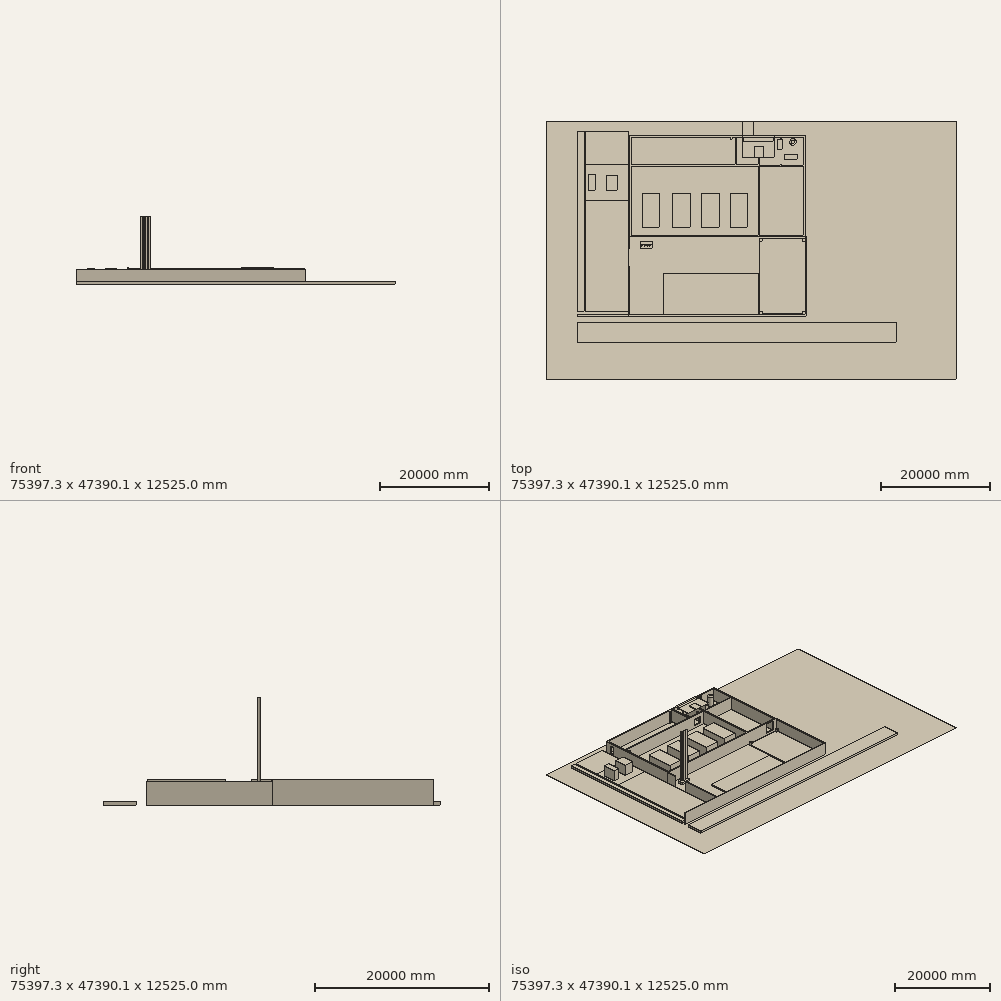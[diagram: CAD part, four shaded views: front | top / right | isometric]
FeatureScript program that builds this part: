
annotation { "Feature Type Name" : "Feature", "Feature Type Description" : "" }
export const myFeature = defineFeature(function(context is Context, id is Id, definition is map)
    precondition{}
    {
        {
            var Q0;
            Q0=qCreatedBy(makeId("Top.planeOp"),FACE);
            var sketch = newSketch(context, id + "F0", { "sketchPlane" : qUnion([Q0])});
            skLineSegment(sketch, "E0.bottom", {"start": v(0, 0) * mm, "end": v(75397.33, 0) * mm});
            skLineSegment(sketch, "E0.top", {"start": v(0, 47390.05) * mm, "end": v(75397.33, 47390.05) * mm});
            skLineSegment(sketch, "E0.left", {"start": v(0, 0) * mm, "end": v(0, 47390.05) * mm});
            skLineSegment(sketch, "E0.right", {"start": v(75397.33, 0) * mm, "end": v(75397.33, 47390.05) * mm});
            skSolve(sketch);
        }
        {
            var Q0;
            Q0 = qSketchRegion(id + "F0", true);
            var Q1;
            Q1=sQuery(id+"F0.wireOp",EDGE,"E0.top");
            var Q2;
            Q2=sQuery(id+"F0.wireOp",EDGE,"E0.left");
            var Q3;
            Q3=sQuery(id+"F0.wireOp",EDGE,"E0.bottom");
            var Q4;
            Q4=sQuery(id+"F0.wireOp",EDGE,"E0.right");
            extrude(context, id + "F1", {"entities" : qUnion([Q0]), "surfaceEntities" : qUnion([Q1, Q2, Q3, Q4]), "depth" : 25 * mm, "offsetDistance" : 25 * mm});
        }
        {
            var Q0;
            Q0=makeQuery(id+"F1.opExtrude","CAP_FACE",FACE,{"disambiguationData":[OSD([sQuery(id+"F0.wireOp",EDGE,"E0.bottom"),sQuery(id+"F0.wireOp",EDGE,"E0.top"),sQuery(id+"F0.wireOp",EDGE,"E0.left"),sQuery(id+"F0.wireOp",EDGE,"E0.right")])],"isStart":false});
            var sketch = newSketch(context, id + "F2", { "sketchPlane" : qUnion([Q0])});
            skLineSegment(sketch, "E1.top", {"start": v(15550.39, 26489.85) * mm, "end": v(38950.39, 26489.85) * mm});
            skLineSegment(sketch, "E1.left", {"start": v(15250.39, 44489.85) * mm, "end": v(15250.39, 39489.85) * mm});
            skLineSegment(sketch, "E1.right", {"start": v(47250.39, 44489.85) * mm, "end": v(47250.39, 26489.85) * mm});
            skLineSegment(sketch, "E2", {"start": v(39250.39, 26489.85) * mm, "end": v(39250.39, 44489.85) * mm});
            skLineSegment(sketch, "E3", {"start": v(15550.39, 39489.85) * mm, "end": v(38950.39, 39489.85) * mm});
            skLineSegment(sketch, "E4", {"start": v(5738.33, 45652.55) * mm, "end": v(5738.33, 12489.85) * mm});
            skLineSegment(sketch, "E5", {"start": v(6911.72, 12489.85) * mm, "end": v(5738.33, 12489.85) * mm});
            skLineSegment(sketch, "E6", {"start": v(5684.42, 10489.85) * mm, "end": v(64413.56, 10489.85) * mm});
            skLineSegment(sketch, "E7", {"start": v(5684.42, 6686.74) * mm, "end": v(64413.56, 6686.74) * mm});
            skLineSegment(sketch, "E8", {"start": v(5684.42, 10489.85) * mm, "end": v(5684.42, 6686.74) * mm});
            skLineSegment(sketch, "E9", {"start": v(64413.56, 10489.85) * mm, "end": v(64413.56, 6686.74) * mm});
            skLineSegment(sketch, "E10", {"start": v(39250.39, 44489.85) * mm, "end": v(47250.39, 44489.85) * mm});
            skLineSegment(sketch, "E11.trimOffspring", {"start": v(39250.39, 26489.85) * mm, "end": v(47250.39, 26489.85) * mm});
            skLineSegment(sketch, "E12", {"start": v(38950.39, 44489.85) * mm, "end": v(15550.39, 44489.85) * mm});
            skLineSegment(sketch, "E13", {"start": v(15550.39, 39189.85) * mm, "end": v(38950.39, 39189.85) * mm});
            skLineSegment(sketch, "E14.trimOffspring", {"start": v(38950.39, 39489.85) * mm, "end": v(38950.39, 44489.85) * mm});
            skLineSegment(sketch, "E15.trimOffspring", {"start": v(15250.39, 39189.85) * mm, "end": v(15250.39, 26489.85) * mm});
            skLineSegment(sketch, "E16.left", {"start": v(6911.72, 45652.55) * mm, "end": v(6911.72, 12489.85) * mm});
            skLineSegment(sketch, "E17.trimOffspring", {"start": v(5738.33, 45652.55) * mm, "end": v(6911.72, 45652.55) * mm});
            skLineSegment(sketch, "E18", {"start": v(15100.39, 12489.85) * mm, "end": v(15100.39, 45621.21) * mm});
            skLineSegment(sketch, "E19.right", {"start": v(8381.05, 13854.85) * mm, "end": v(8381.05, 13847.74) * mm});
            skLineSegment(sketch, "E20.top", {"start": v(15250.39, 44789.85) * mm, "end": v(47550.39, 44789.85) * mm});
            skLineSegment(sketch, "E21", {"start": v(15250.39, 26189.85) * mm, "end": v(15250.39, 44789.85) * mm});
            skLineSegment(sketch, "E22", {"start": v(7100.39, 45621.21) * mm, "end": v(15100.39, 45621.21) * mm});
            skLineSegment(sketch, "E23.trimOffspring", {"start": v(7100.39, 45621.21) * mm, "end": v(7100.39, 12489.85) * mm});
            skLineSegment(sketch, "E24", {"start": v(7100.39, 12489.85) * mm, "end": v(15100.39, 12489.85) * mm});
            skLineSegment(sketch, "E25", {"start": v(39250.39, 39189.85) * mm, "end": v(39250.39, 26489.85) * mm});
            skLineSegment(sketch, "E26", {"start": v(47550.39, 44789.85) * mm, "end": v(47550.39, 26189.85) * mm});
            skLineSegment(sketch, "E27", {"start": v(47550.39, 26189.85) * mm, "end": v(15250.39, 26189.85) * mm});
            skLineSegment(sketch, "E28", {"start": v(38950.39, 26489.85) * mm, "end": v(38950.39, 39189.85) * mm});
            skLineSegment(sketch, "E29", {"start": v(15550.39, 26489.85) * mm, "end": v(15550.39, 39189.85) * mm});
            skLineSegment(sketch, "E30", {"start": v(15550.39, 44489.85) * mm, "end": v(15550.39, 39489.85) * mm});
            skLineSegment(sketch, "E31.bottom", {"start": v(17308.66, 25290.44) * mm, "end": v(19540.62, 25290.44) * mm});
            skLineSegment(sketch, "E31.top", {"start": v(17308.66, 23988.97) * mm, "end": v(19540.62, 23988.97) * mm});
            skLineSegment(sketch, "E31.left", {"start": v(17308.66, 25290.44) * mm, "end": v(17308.66, 23988.97) * mm});
            skLineSegment(sketch, "E31.right", {"start": v(19540.62, 25290.44) * mm, "end": v(19540.62, 23988.97) * mm});
            skSolve(sketch);
        }
        {
            var Q0;
            Q0=makeQuery(id+"F2.imprint","IMPRINT",FACE,{"disambiguationData":[TD([[makeQuery(id+"F2.imprint","IMPRINT",EDGE,{"derivedFrom":sQuery(id+"F2.wireOp",EDGE,"E1.top")}),-1.0]])]});
            extrude(context, id + "F3", {"entities" : qUnion([Q0]), "operationType" : NewBodyOperationType.ADD, "depth" : 3000 * mm, "offsetDistance" : 25 * mm});
        }
        {
            var Q0;
            {var subQ0=sQuery(id+"F0.wireOp",EDGE,"E0.left");var subQ1=sQuery(id+"F0.wireOp",EDGE,"E0.top");var subQ2=sQuery(id+"F0.wireOp",EDGE,"E0.right");var subQ3=sQuery(id+"F0.wireOp",EDGE,"E0.bottom");Q0=makeQuery(id+"F3.boolean.opBoolean","SPLIT",FACE,{"disambiguationData":[TD([makeQuery(id+"F1.opExtrude","SWEPT_FACE",FACE,{"disambiguationData":[OSD([subQ3])]})])],"derivedFrom":makeQuery(id+"F1.opExtrude","CAP_FACE",FACE,{"disambiguationData":[OSD([subQ3,subQ1,subQ0,subQ2])],"isStart":false})});}
            var sketch = newSketch(context, id + "F4", { "sketchPlane" : qUnion([Q0])});
            skLineSegment(sketch, "E32.bottom", {"start": v(47550.39, 25889.85) * mm, "end": v(39250.39, 25889.85) * mm});
            skLineSegment(sketch, "E32.top", {"start": v(47550.39, 11889.85) * mm, "end": v(39250.39, 11889.85) * mm});
            skLineSegment(sketch, "E32.left", {"start": v(47550.39, 25889.85) * mm, "end": v(47550.39, 11889.85) * mm});
            skLineSegment(sketch, "E32.right", {"start": v(39250.39, 25889.85) * mm, "end": v(39250.39, 11889.85) * mm});
            skSolve(sketch);
        }
        {
            var Q0;
            Q0=makeQuery(id+"F4.imprint","IMPRINT",FACE,{"disambiguationData":[TD([[makeQuery(id+"F4.imprint","IMPRINT",EDGE,{"derivedFrom":sQuery(id+"F4.wireOp",EDGE,"E32.bottom")}),1.0]])]});
            var Q1;
            Q1=sQuery(id+"F4.wireOp",EDGE,"E32.right");
            var Q2;
            Q2=sQuery(id+"F4.wireOp",EDGE,"E32.top");
            var Q3;
            Q3=sQuery(id+"F4.wireOp",EDGE,"E32.left");
            var Q4;
            Q4=sQuery(id+"F4.wireOp",EDGE,"E32.bottom");
            extrude(context, id + "F5", {"entities" : qUnion([Q0]), "surfaceEntities" : qUnion([Q1, Q2, Q3, Q4]), "depth" : 200 * mm, "offsetDistance" : 25 * mm});
        }
        {
            var Q0;
            Q0 = qSketchRegion(id + "F2", true);
            var Q1;
            {var subQ0=sQuery(id+"F0.wireOp",EDGE,"E0.left");var subQ1=sQuery(id+"F0.wireOp",EDGE,"E0.top");var subQ2=sQuery(id+"F0.wireOp",EDGE,"E0.right");var subQ3=sQuery(id+"F0.wireOp",EDGE,"E0.bottom");Q1=makeQuery(id+"F3.boolean.opBoolean","SPLIT",FACE,{"disambiguationData":[TD([makeQuery(id+"F1.opExtrude","SWEPT_FACE",FACE,{"disambiguationData":[OSD([subQ3])]})])],"derivedFrom":makeQuery(id+"F1.opExtrude","CAP_FACE",FACE,{"disambiguationData":[OSD([subQ3,subQ1,subQ0,subQ2])],"isStart":false})});}
            extrude(context, id + "F6", {"entities" : qUnion([Q0, Q1]), "operationType" : NewBodyOperationType.ADD, "depth" : 25 * mm, "offsetDistance" : 25 * mm});
        }
        {
            var Q0;
            Q0 = qSketchRegion(id + "F2", true);
            extrude(context, id + "F7", {"entities" : qUnion([Q0]), "operationType" : NewBodyOperationType.ADD, "depth" : 200 * mm, "offsetDistance" : 25 * mm});
        }
        {
            var Q0;
            {var subQ0=sQuery(id+"F2.wireOp",EDGE,"d6d11424-035c-424b-929e-fb8eabbb2fd0.right");var subQ1=sQuery(id+"F2.wireOp",EDGE,"d6d11424-035c-424b-929e-fb8eabbb2fd0.bottom");var subQ2=sQuery(id+"F2.wireOp",EDGE,"E9");var subQ3=sQuery(id+"F2.wireOp",EDGE,"E8");var subQ4=sQuery(id+"F2.wireOp",EDGE,"E7");var subQ5=sQuery(id+"F2.wireOp",EDGE,"E6");var subQ6=sQuery(id+"F2.wireOp",EDGE,"E5");var subQ7=sQuery(id+"F0.wireOp",EDGE,"E0.right");var subQ8=sQuery(id+"F2.wireOp",EDGE,"d6d11424-035c-424b-929e-fb8eabbb2fd0.left");var subQ9=sQuery(id+"F2.wireOp",EDGE,"E27");var subQ10=sQuery(id+"F2.wireOp",EDGE,"E16.left");var subQ11=sQuery(id+"F2.wireOp",EDGE,"d6d11424-035c-424b-929e-fb8eabbb2fd0.top");var subQ12=sQuery(id+"F2.wireOp",EDGE,"E26");var subQ13=sQuery(id+"F0.wireOp",EDGE,"E0.left");var subQ14=sQuery(id+"F0.wireOp",EDGE,"E0.bottom");var subQ15=sQuery(id+"F2.wireOp",EDGE,"E4");var subQ16=sQuery(id+"F2.wireOp",EDGE,"E24");var subQ17=sQuery(id+"F0.wireOp",EDGE,"E0.top");var subQ18=sQuery(id+"F2.wireOp",EDGE,"E20.top");var subQ19=sQuery(id+"F2.wireOp",EDGE,"E21");var subQ20=sQuery(id+"F2.wireOp",EDGE,"E23.trimOffspring");var subQ21=sQuery(id+"F2.wireOp",EDGE,"E17.trimOffspring");var subQ22=sQuery(id+"F2.wireOp",EDGE,"E18");var subQ23=sQuery(id+"F2.wireOp",EDGE,"E22");Q0=makeQuery(id+"F7.boolean.opBoolean","SPLIT",FACE,{"disambiguationData":[TD([makeQuery(id+"F1.opExtrude","SWEPT_FACE",FACE,{"disambiguationData":[OSD([subQ14])]})])],"derivedFrom":makeQuery(id+"F6.boolean.opBoolean","MERGE",FACE,{"derivedFrom":[makeQuery(id+"F6.opExtrude","CAP_FACE",FACE,{"disambiguationData":[OSD([sQuery(id+"F2.wireOp",EDGE,"E1.top"),sQuery(id+"F2.wireOp",EDGE,"E1.right"),sQuery(id+"F2.wireOp",EDGE,"E2"),sQuery(id+"F2.wireOp",EDGE,"E3"),sQuery(id+"F2.wireOp",EDGE,"E10"),sQuery(id+"F2.wireOp",EDGE,"E11.trimOffspring"),sQuery(id+"F2.wireOp",EDGE,"E12"),sQuery(id+"F2.wireOp",EDGE,"E13"),sQuery(id+"F2.wireOp",EDGE,"E14.trimOffspring"),subQ18,subQ19,sQuery(id+"F2.wireOp",EDGE,"E25"),subQ12,subQ9,sQuery(id+"F2.wireOp",EDGE,"E28"),sQuery(id+"F2.wireOp",EDGE,"E29"),sQuery(id+"F2.wireOp",EDGE,"E30")])],"isStart":false}),makeQuery(id+"F6.opExtrude","CAP_FACE",FACE,{"disambiguationData":[OSD([subQ15,subQ6,subQ10,subQ21])],"isStart":false}),makeQuery(id+"F6.opExtrude","CAP_FACE",FACE,{"disambiguationData":[OSD([subQ5,subQ4,subQ3,subQ2])],"isStart":false}),makeQuery(id+"F6.opExtrude","CAP_FACE",FACE,{"disambiguationData":[OSD([subQ1,subQ11,subQ8,subQ0,sQuery(id+"F2.wireOp",EDGE,"95qXsgm3-6lwU-iEXp-UI7w-R3bsq3icprrx.bottom"),sQuery(id+"F2.wireOp",EDGE,"95qXsgm3-6lwU-iEXp-UI7w-R3bsq3icprrx.top"),sQuery(id+"F2.wireOp",EDGE,"95qXsgm3-6lwU-iEXp-UI7w-R3bsq3icprrx.left"),sQuery(id+"F2.wireOp",EDGE,"95qXsgm3-6lwU-iEXp-UI7w-R3bsq3icprrx.right")])],"isStart":false}),makeQuery(id+"F6.opExtrude","CAP_FACE",FACE,{"disambiguationData":[OSD([subQ22,subQ23,subQ20,subQ16])],"isStart":false}),makeQuery(id+"F6.opExtrude","CAP_FACE",FACE,{"disambiguationData":[OSD([subQ14,subQ17,subQ13,subQ7])],"isStart":false})]})});}
            var sketch = newSketch(context, id + "F8", { "sketchPlane" : qUnion([Q0])});
            skLineSegment(sketch, "E33.bottom", {"start": v(38899.38, 19555.93) * mm, "end": v(21486.93, 19555.93) * mm});
            skLineSegment(sketch, "E33.top", {"start": v(38899.38, 11971.84) * mm, "end": v(21486.93, 11971.84) * mm});
            skLineSegment(sketch, "E33.left", {"start": v(38899.38, 19555.93) * mm, "end": v(38899.38, 11971.84) * mm});
            skLineSegment(sketch, "E33.right", {"start": v(21486.93, 19555.93) * mm, "end": v(21486.93, 11971.84) * mm});
            skSolve(sketch);
        }
        {
            var Q0;
            Q0 = qSketchRegion(id + "F8", true);
            extrude(context, id + "F9", {"entities" : qUnion([Q0]), "operationType" : NewBodyOperationType.ADD, "depth" : 200 * mm, "offsetDistance" : 25 * mm});
        }
        {
            var Q0;
            Q0=makeQuery(id+"F3.opExtrude","SWEPT_FACE",FACE,{"disambiguationData":[OSD([sQuery(id+"F2.wireOp",EDGE,"E27")])]});
            var sketch = newSketch(context, id + "F10", { "sketchPlane" : qUnion([Q0])});
            skLineSegment(sketch, "E34.bottom", {"start": v(44814.1, 2729.8) * mm, "end": v(46814.1, 2729.8) * mm});
            skLineSegment(sketch, "E34.top", {"start": v(44814.1, 229.8) * mm, "end": v(46814.1, 229.8) * mm});
            skLineSegment(sketch, "E34.left", {"start": v(44814.1, 2729.8) * mm, "end": v(44814.1, 229.8) * mm});
            skLineSegment(sketch, "E34.right", {"start": v(46814.1, 2729.8) * mm, "end": v(46814.1, 229.8) * mm});
            skSolve(sketch);
        }
        {
            var Q0;
            Q0=makeQuery(id+"F10.imprint","IMPRINT",FACE,{"disambiguationData":[TD([[makeQuery(id+"F10.imprint","IMPRINT",EDGE,{"derivedFrom":sQuery(id+"F10.wireOp",EDGE,"E34.bottom")}),-1.0]])]});
            extrude(context, id + "F11", {"entities" : qUnion([Q0]), "operationType" : NewBodyOperationType.REMOVE, "oppositeDirection" : true, "depth" : 400 * mm, "offsetDistance" : 25 * mm});
        }
        {
            var Q0;
            Q0=makeQuery(id+"F3.opExtrude","SWEPT_FACE",FACE,{"disambiguationData":[OSD([sQuery(id+"F2.wireOp",EDGE,"E2"),sQuery(id+"F2.wireOp",EDGE,"E25")])]});
            var sketch = newSketch(context, id + "F12", { "sketchPlane" : qUnion([Q0])});
            skLineSegment(sketch, "E35.bottom", {"start": v(40270.04, 2225) * mm, "end": v(41470.04, 2225) * mm});
            skLineSegment(sketch, "E35.top", {"start": v(40270.04, 25) * mm, "end": v(41470.04, 25) * mm});
            skLineSegment(sketch, "E35.left", {"start": v(40270.04, 2225) * mm, "end": v(40270.04, 25) * mm});
            skLineSegment(sketch, "E35.right", {"start": v(41470.04, 2225) * mm, "end": v(41470.04, 25) * mm});
            skSolve(sketch);
        }
        {
            var Q0;
            Q0 = qSketchRegion(id + "F12", true);
            extrude(context, id + "F13", {"entities" : qUnion([Q0]), "operationType" : NewBodyOperationType.REMOVE, "oppositeDirection" : true, "depth" : 310 * mm, "offsetDistance" : 25 * mm});
        }
        {
            var Q0;
            Q0=makeQuery(id+"F3.opExtrude","SWEPT_FACE",FACE,{"disambiguationData":[OSD([sQuery(id+"F2.wireOp",EDGE,"E21")])]});
            var sketch = newSketch(context, id + "F14", { "sketchPlane" : qUnion([Q0])});
            skLineSegment(sketch, "E36.bottom", {"start": v(-43520.03, 2405.42) * mm, "end": v(-42542.72, 2405.42) * mm});
            skLineSegment(sketch, "E36.top", {"start": v(-43520.03, 220.95) * mm, "end": v(-42542.72, 220.95) * mm});
            skLineSegment(sketch, "E36.left", {"start": v(-43520.03, 2405.42) * mm, "end": v(-43520.03, 220.95) * mm});
            skLineSegment(sketch, "E36.right", {"start": v(-42542.72, 2405.42) * mm, "end": v(-42542.72, 220.95) * mm});
            skSolve(sketch);
        }
        {
            var Q0;
            Q0 = qSketchRegion(id + "F14", true);
            extrude(context, id + "F15", {"entities" : qUnion([Q0]), "operationType" : NewBodyOperationType.REMOVE, "oppositeDirection" : true, "depth" : 305 * mm, "offsetDistance" : 25 * mm});
        }
        {
            var Q0;
            Q0=makeQuery(id+"F5.opExtrude","CAP_FACE",FACE,{"disambiguationData":[OSD([sQuery(id+"F4.wireOp",EDGE,"E32.bottom"),sQuery(id+"F4.wireOp",EDGE,"E32.top"),sQuery(id+"F4.wireOp",EDGE,"E32.left"),sQuery(id+"F4.wireOp",EDGE,"E32.right")])],"isStart":false});
            var sketch = newSketch(context, id + "F16", { "sketchPlane" : qUnion([Q0])});
            skLineSegment(sketch, "E37.bottom", {"start": v(47550.39, 11889.85) * mm, "end": v(47050.39, 11889.85) * mm});
            skLineSegment(sketch, "E37.top", {"start": v(47550.39, 12389.85) * mm, "end": v(47050.39, 12389.85) * mm});
            skLineSegment(sketch, "E37.left", {"start": v(47550.39, 11889.85) * mm, "end": v(47550.39, 12389.85) * mm});
            skLineSegment(sketch, "E37.right", {"start": v(47050.39, 11889.85) * mm, "end": v(47050.39, 12389.85) * mm});
            skLineSegment(sketch, "E38.bottom", {"start": v(39250.39, 11889.85) * mm, "end": v(39705.44, 11889.85) * mm});
            skLineSegment(sketch, "E38.top", {"start": v(39250.39, 12389.85) * mm, "end": v(39705.44, 12389.85) * mm});
            skLineSegment(sketch, "E38.left", {"start": v(39250.39, 11889.85) * mm, "end": v(39250.39, 12389.85) * mm});
            skLineSegment(sketch, "E38.right", {"start": v(39705.44, 11889.85) * mm, "end": v(39705.44, 12389.85) * mm});
            skLineSegment(sketch, "E39.bottom", {"start": v(39250.39, 25889.85) * mm, "end": v(39750.39, 25889.85) * mm});
            skLineSegment(sketch, "E39.top", {"start": v(39250.39, 25389.85) * mm, "end": v(39750.39, 25389.85) * mm});
            skLineSegment(sketch, "E39.left", {"start": v(39250.39, 25889.85) * mm, "end": v(39250.39, 25389.85) * mm});
            skLineSegment(sketch, "E39.right", {"start": v(39750.39, 25889.85) * mm, "end": v(39750.39, 25389.85) * mm});
            skLineSegment(sketch, "E40.bottom", {"start": v(47550.39, 25889.85) * mm, "end": v(47050.39, 25889.85) * mm});
            skLineSegment(sketch, "E40.top", {"start": v(47550.39, 25389.85) * mm, "end": v(47050.39, 25389.85) * mm});
            skLineSegment(sketch, "E40.left", {"start": v(47550.39, 25889.85) * mm, "end": v(47550.39, 25389.85) * mm});
            skLineSegment(sketch, "E40.right", {"start": v(47050.39, 25889.85) * mm, "end": v(47050.39, 25389.85) * mm});
            skSolve(sketch);
        }
        {
            var Q0;
            Q0 = qSketchRegion(id + "F16", true);
            extrude(context, id + "F17", {"entities" : qUnion([Q0]), "operationType" : NewBodyOperationType.ADD, "depth" : 600 * mm, "offsetDistance" : 25 * mm});
        }
        {
            var Q0;
            Q0=makeQuery(id+"F3.opExtrude","SWEPT_FACE",FACE,{"disambiguationData":[OSD([sQuery(id+"F2.wireOp",EDGE,"E13")])]});
            var sketch = newSketch(context, id + "F18", { "sketchPlane" : qUnion([Q0])});
            skLineSegment(sketch, "E41.bottom", {"start": v(15908.28, 25) * mm, "end": v(16820.83, 25) * mm});
            skLineSegment(sketch, "E41.top", {"start": v(15908.28, 2525) * mm, "end": v(16820.83, 2525) * mm});
            skLineSegment(sketch, "E41.left", {"start": v(15908.28, 25) * mm, "end": v(15908.28, 2525) * mm});
            skLineSegment(sketch, "E41.right", {"start": v(16820.83, 25) * mm, "end": v(16820.83, 2525) * mm});
            skSolve(sketch);
        }
        {
            var Q0;
            Q0 = qSketchRegion(id + "F18", true);
            extrude(context, id + "F19", {"entities" : qUnion([Q0]), "operationType" : NewBodyOperationType.REMOVE, "oppositeDirection" : true, "depth" : 310 * mm, "offsetDistance" : 25 * mm});
        }
        {
            var Q0;
            {var subQ0=makeQuery(id+"F1.opExtrude","CAP_FACE",FACE,{"disambiguationData":[OSD([sQuery(id+"F0.wireOp",EDGE,"E0.bottom"),sQuery(id+"F0.wireOp",EDGE,"E0.top"),sQuery(id+"F0.wireOp",EDGE,"E0.left"),sQuery(id+"F0.wireOp",EDGE,"E0.right")])],"isStart":false});Q0=makeQuery(id+"F19.boolean.opBoolean","MERGE",FACE,{"derivedFrom":[makeQuery(id+"F3.boolean.opBoolean","SPLIT",FACE,{"disambiguationData":[TD([makeQuery(id+"F3.opExtrude","SWEPT_FACE",FACE,{"disambiguationData":[OSD([sQuery(id+"F2.wireOp",EDGE,"E1.top")])]})])],"derivedFrom":subQ0}),makeQuery(id+"F13.boolean.opBoolean","MERGE",FACE,{"derivedFrom":[makeQuery(id+"F3.boolean.opBoolean","SPLIT",FACE,{"disambiguationData":[TD([makeQuery(id+"F3.opExtrude","SWEPT_FACE",FACE,{"disambiguationData":[OSD([sQuery(id+"F2.wireOp",EDGE,"E1.right")])]})])],"derivedFrom":subQ0}),makeQuery(id+"F3.boolean.opBoolean","SPLIT",FACE,{"disambiguationData":[TD([makeQuery(id+"F3.opExtrude","SWEPT_FACE",FACE,{"disambiguationData":[OSD([sQuery(id+"F2.wireOp",EDGE,"E3")])]})])],"derivedFrom":subQ0}),makeQuery(id+"F13.opExtrude","SWEPT_FACE",FACE,{"disambiguationData":[OSD([sQuery(id+"F12.wireOp",EDGE,"E35.top")])]})]}),makeQuery(id+"F19.opExtrude","SWEPT_FACE",FACE,{"disambiguationData":[OSD([sQuery(id+"F18.wireOp",EDGE,"E41.bottom")])]})]});}
            var sketch = newSketch(context, id + "F20", { "sketchPlane" : qUnion([Q0])});
            skLineSegment(sketch, "E42.bottom", {"start": v(43250.39, 44489.85) * mm, "end": v(42950.39, 44489.85) * mm});
            skLineSegment(sketch, "E42.top", {"start": v(43250.39, 44189.85) * mm, "end": v(42950.39, 44189.85) * mm});
            skLineSegment(sketch, "E42.left", {"start": v(43250.39, 44489.85) * mm, "end": v(43250.39, 44189.85) * mm});
            skLineSegment(sketch, "E42.right", {"start": v(42950.39, 44489.85) * mm, "end": v(42950.39, 44189.85) * mm});
            skLineSegment(sketch, "E43.bottom", {"start": v(43250.39, 39511.55) * mm, "end": v(42950.39, 39511.55) * mm});
            skLineSegment(sketch, "E43.top", {"start": v(43250.39, 39211.55) * mm, "end": v(42950.39, 39211.55) * mm});
            skLineSegment(sketch, "E43.left", {"start": v(43250.39, 39511.55) * mm, "end": v(43250.39, 39211.55) * mm});
            skLineSegment(sketch, "E43.right", {"start": v(42950.39, 39511.55) * mm, "end": v(42950.39, 39211.55) * mm});
            skLineSegment(sketch, "E44.bottom", {"start": v(33845.83, 39511.55) * mm, "end": v(34145.83, 39511.55) * mm});
            skLineSegment(sketch, "E44.top", {"start": v(33845.83, 39211.55) * mm, "end": v(34145.83, 39211.55) * mm});
            skLineSegment(sketch, "E44.left", {"start": v(33845.83, 39511.55) * mm, "end": v(33845.83, 39211.55) * mm});
            skLineSegment(sketch, "E44.right", {"start": v(34145.83, 39511.55) * mm, "end": v(34145.83, 39211.55) * mm});
            skLineSegment(sketch, "E45.bottom", {"start": v(33845.83, 44489.85) * mm, "end": v(34145.83, 44489.85) * mm});
            skLineSegment(sketch, "E45.top", {"start": v(33845.83, 44189.85) * mm, "end": v(34145.83, 44189.85) * mm});
            skLineSegment(sketch, "E45.left", {"start": v(33845.83, 44489.85) * mm, "end": v(33845.83, 44189.85) * mm});
            skLineSegment(sketch, "E45.right", {"start": v(34145.83, 44489.85) * mm, "end": v(34145.83, 44189.85) * mm});
            skSolve(sketch);
        }
        {
            var Q0;
            Q0=makeQuery(id+"F20.imprint","IMPRINT",FACE,{"disambiguationData":[TD([[makeQuery(id+"F20.imprint","IMPRINT",EDGE,{"derivedFrom":sQuery(id+"F20.wireOp",EDGE,"E42.bottom")}),-1.0]])]});
            var Q1;
            Q1=makeQuery(id+"F20.imprint","IMPRINT",FACE,{"disambiguationData":[TD([[makeQuery(id+"F20.imprint","IMPRINT",EDGE,{"derivedFrom":sQuery(id+"F20.wireOp",EDGE,"E43.bottom")}),1.0]])]});
            var Q2;
            {var subQ0=sQuery(id+"F20.wireOp",EDGE,"E44.bottom");Q2=makeQuery(id+"F20.imprint","IMPRINT",FACE,{"disambiguationData":[TD([[makeQuery(id+"F20.imprint","IMPRINT",EDGE,{"derivedFrom":subQ0}),-1.0]])]});}
            var Q3;
            Q3=makeQuery(id+"F20.imprint","IMPRINT",FACE,{"disambiguationData":[TD([[makeQuery(id+"F20.imprint","IMPRINT",EDGE,{"derivedFrom":sQuery(id+"F20.wireOp",EDGE,"E45.bottom")}),1.0]])]});
            extrude(context, id + "F21", {"entities" : qUnion([Q0, Q1, Q2, Q3]), "operationType" : NewBodyOperationType.ADD, "depth" : 3000 * mm, "offsetDistance" : 25 * mm});
        }
        {
            var Q0;
            Q0=makeQuery(id+"F3.opExtrude","SWEPT_FACE",FACE,{"disambiguationData":[OSD([sQuery(id+"F2.wireOp",EDGE,"E13")])]});
            var sketch = newSketch(context, id + "F22", { "sketchPlane" : qUnion([Q0])});
            skLineSegment(sketch, "E46.bottom", {"start": v(35990.2, 2225) * mm, "end": v(37990.2, 2225) * mm});
            skLineSegment(sketch, "E46.top", {"start": v(35990.2, 25) * mm, "end": v(37990.2, 25) * mm});
            skLineSegment(sketch, "E46.left", {"start": v(35990.2, 2225) * mm, "end": v(35990.2, 25) * mm});
            skLineSegment(sketch, "E46.right", {"start": v(37990.2, 2225) * mm, "end": v(37990.2, 25) * mm});
            skSolve(sketch);
        }
        {
            var Q0;
            Q0 = qSketchRegion(id + "F22", true);
            extrude(context, id + "F23", {"entities" : qUnion([Q0]), "operationType" : NewBodyOperationType.REMOVE, "endBound" : BoundingType.THROUGH_ALL, "oppositeDirection" : true, "depth" : 25 * mm, "offsetDistance" : 25 * mm});
        }
        {
            var Q0;
            Q0=makeQuery(id+"F5.opExtrude","CAP_FACE",FACE,{"disambiguationData":[OSD([sQuery(id+"F4.wireOp",EDGE,"E32.bottom"),sQuery(id+"F4.wireOp",EDGE,"E32.top"),sQuery(id+"F4.wireOp",EDGE,"E32.left"),sQuery(id+"F4.wireOp",EDGE,"E32.right")])],"isStart":false});
            var sketch = newSketch(context, id + "F24", { "sketchPlane" : qUnion([Q0])});
            skLineSegment(sketch, "E47.bottom", {"start": v(39705.44, 12139.85) * mm, "end": v(47050.39, 12139.85) * mm});
            skLineSegment(sketch, "E47.top", {"start": v(39705.44, 12139.85) * mm, "end": v(47050.39, 12139.85) * mm});
            skLineSegment(sketch, "E47.left", {"start": v(39705.44, 12139.85) * mm, "end": v(39705.44, 12139.85) * mm});
            skLineSegment(sketch, "E47.right", {"start": v(47050.39, 12139.85) * mm, "end": v(47050.39, 12139.85) * mm});
            skLineSegment(sketch, "E48.bottom", {"start": v(47050.39, 11889.85) * mm, "end": v(39705.44, 11889.85) * mm});
            skLineSegment(sketch, "E48.top", {"start": v(47050.39, 12139.85) * mm, "end": v(39705.44, 12139.85) * mm});
            skLineSegment(sketch, "E48.left", {"start": v(47050.39, 11889.85) * mm, "end": v(47050.39, 12139.85) * mm});
            skLineSegment(sketch, "E48.right", {"start": v(39705.44, 11889.85) * mm, "end": v(39705.44, 12139.85) * mm});
            skSolve(sketch);
        }
        {
            var Q0;
            Q0 = qSketchRegion(id + "F24", true);
            var Q1;
            Q1=makeQuery(id+"F24.imprint","IMPRINT",FACE,{"disambiguationData":[TD([[makeQuery(id+"F24.imprint","IMPRINT",EDGE,{"derivedFrom":sQuery(id+"F24.wireOp",EDGE,"E48.bottom")}),-1.0]])]});
            extrude(context, id + "F25", {"entities" : qUnion([Q0, Q1]), "operationType" : NewBodyOperationType.ADD, "depth" : 1000 * mm, "offsetDistance" : 25 * mm});
        }
        {
            var Q0;
            {var subQ0=sQuery(id+"F2.wireOp",EDGE,"d6d11424-035c-424b-929e-fb8eabbb2fd0.right");var subQ1=sQuery(id+"F2.wireOp",EDGE,"d6d11424-035c-424b-929e-fb8eabbb2fd0.bottom");var subQ2=sQuery(id+"F2.wireOp",EDGE,"E9");var subQ3=sQuery(id+"F2.wireOp",EDGE,"E8");var subQ4=sQuery(id+"F2.wireOp",EDGE,"E7");var subQ5=sQuery(id+"F2.wireOp",EDGE,"E6");var subQ6=sQuery(id+"F2.wireOp",EDGE,"E5");var subQ7=sQuery(id+"F0.wireOp",EDGE,"E0.right");var subQ8=sQuery(id+"F2.wireOp",EDGE,"d6d11424-035c-424b-929e-fb8eabbb2fd0.left");var subQ9=sQuery(id+"F2.wireOp",EDGE,"E27");var subQ10=sQuery(id+"F2.wireOp",EDGE,"E16.left");var subQ11=sQuery(id+"F2.wireOp",EDGE,"d6d11424-035c-424b-929e-fb8eabbb2fd0.top");var subQ12=sQuery(id+"F2.wireOp",EDGE,"E26");var subQ13=sQuery(id+"F0.wireOp",EDGE,"E0.left");var subQ14=sQuery(id+"F0.wireOp",EDGE,"E0.bottom");var subQ15=sQuery(id+"F2.wireOp",EDGE,"E4");var subQ16=sQuery(id+"F2.wireOp",EDGE,"E24");var subQ17=sQuery(id+"F0.wireOp",EDGE,"E0.top");var subQ18=sQuery(id+"F2.wireOp",EDGE,"E20.top");var subQ19=sQuery(id+"F2.wireOp",EDGE,"E21");var subQ20=sQuery(id+"F2.wireOp",EDGE,"E23.trimOffspring");var subQ21=sQuery(id+"F2.wireOp",EDGE,"E17.trimOffspring");var subQ22=sQuery(id+"F2.wireOp",EDGE,"E18");var subQ23=sQuery(id+"F2.wireOp",EDGE,"E22");Q0=makeQuery(id+"F7.boolean.opBoolean","SPLIT",FACE,{"disambiguationData":[TD([makeQuery(id+"F1.opExtrude","SWEPT_FACE",FACE,{"disambiguationData":[OSD([subQ14])]})])],"derivedFrom":makeQuery(id+"F6.boolean.opBoolean","MERGE",FACE,{"derivedFrom":[makeQuery(id+"F6.opExtrude","CAP_FACE",FACE,{"disambiguationData":[OSD([sQuery(id+"F2.wireOp",EDGE,"E1.top"),sQuery(id+"F2.wireOp",EDGE,"E1.right"),sQuery(id+"F2.wireOp",EDGE,"E2"),sQuery(id+"F2.wireOp",EDGE,"E3"),sQuery(id+"F2.wireOp",EDGE,"E10"),sQuery(id+"F2.wireOp",EDGE,"E11.trimOffspring"),sQuery(id+"F2.wireOp",EDGE,"E12"),sQuery(id+"F2.wireOp",EDGE,"E13"),sQuery(id+"F2.wireOp",EDGE,"E14.trimOffspring"),subQ18,subQ19,sQuery(id+"F2.wireOp",EDGE,"E25"),subQ12,subQ9,sQuery(id+"F2.wireOp",EDGE,"E28"),sQuery(id+"F2.wireOp",EDGE,"E29"),sQuery(id+"F2.wireOp",EDGE,"E30")])],"isStart":false}),makeQuery(id+"F6.opExtrude","CAP_FACE",FACE,{"disambiguationData":[OSD([subQ15,subQ6,subQ10,subQ21])],"isStart":false}),makeQuery(id+"F6.opExtrude","CAP_FACE",FACE,{"disambiguationData":[OSD([subQ5,subQ4,subQ3,subQ2])],"isStart":false}),makeQuery(id+"F6.opExtrude","CAP_FACE",FACE,{"disambiguationData":[OSD([subQ1,subQ11,subQ8,subQ0,sQuery(id+"F2.wireOp",EDGE,"95qXsgm3-6lwU-iEXp-UI7w-R3bsq3icprrx.bottom"),sQuery(id+"F2.wireOp",EDGE,"95qXsgm3-6lwU-iEXp-UI7w-R3bsq3icprrx.top"),sQuery(id+"F2.wireOp",EDGE,"95qXsgm3-6lwU-iEXp-UI7w-R3bsq3icprrx.left"),sQuery(id+"F2.wireOp",EDGE,"95qXsgm3-6lwU-iEXp-UI7w-R3bsq3icprrx.right")])],"isStart":false}),makeQuery(id+"F6.opExtrude","CAP_FACE",FACE,{"disambiguationData":[OSD([subQ22,subQ23,subQ20,subQ16])],"isStart":false}),makeQuery(id+"F6.opExtrude","CAP_FACE",FACE,{"disambiguationData":[OSD([subQ14,subQ17,subQ13,subQ7])],"isStart":false})]})});}
            var sketch = newSketch(context, id + "F26", { "sketchPlane" : qUnion([Q0])});
            skLineSegment(sketch, "E49.bottom", {"start": v(47800.39, 11638.85) * mm, "end": v(5738.33, 11638.85) * mm});
            skLineSegment(sketch, "E49.top", {"start": v(47550.39, 11888.85) * mm, "end": v(5738.33, 11888.85) * mm});
            skLineSegment(sketch, "E49.left", {"start": v(47800.39, 11638.85) * mm, "end": v(47800.39, 11888.85) * mm});
            skLineSegment(sketch, "E49.right", {"start": v(5738.33, 11638.85) * mm, "end": v(5738.33, 11888.85) * mm});
            skLineSegment(sketch, "E50.bottom", {"start": v(47800.39, 11638.85) * mm, "end": v(47550.39, 11638.85) * mm});
            skLineSegment(sketch, "E50.top", {"start": v(47800.39, 26189.85) * mm, "end": v(47550.39, 26189.85) * mm});
            skLineSegment(sketch, "E50.left", {"start": v(47800.39, 11638.85) * mm, "end": v(47800.39, 26189.85) * mm});
            skLineSegment(sketch, "E50.right", {"start": v(47550.39, 11888.85) * mm, "end": v(47550.39, 26189.85) * mm});
            skSolve(sketch);
        }
        {
            var Q0;
            {var subQ0=sQuery(id+"F2.wireOp",EDGE,"d6d11424-035c-424b-929e-fb8eabbb2fd0.right");var subQ1=sQuery(id+"F2.wireOp",EDGE,"d6d11424-035c-424b-929e-fb8eabbb2fd0.bottom");var subQ2=sQuery(id+"F2.wireOp",EDGE,"E9");var subQ3=sQuery(id+"F2.wireOp",EDGE,"E8");var subQ4=sQuery(id+"F2.wireOp",EDGE,"E7");var subQ5=sQuery(id+"F2.wireOp",EDGE,"E6");var subQ6=sQuery(id+"F2.wireOp",EDGE,"E5");var subQ7=sQuery(id+"F0.wireOp",EDGE,"E0.right");var subQ8=sQuery(id+"F2.wireOp",EDGE,"d6d11424-035c-424b-929e-fb8eabbb2fd0.left");var subQ9=sQuery(id+"F2.wireOp",EDGE,"E27");var subQ10=sQuery(id+"F2.wireOp",EDGE,"E16.left");var subQ11=sQuery(id+"F2.wireOp",EDGE,"d6d11424-035c-424b-929e-fb8eabbb2fd0.top");var subQ12=sQuery(id+"F2.wireOp",EDGE,"E26");var subQ13=sQuery(id+"F0.wireOp",EDGE,"E0.left");var subQ14=sQuery(id+"F0.wireOp",EDGE,"E0.bottom");var subQ15=sQuery(id+"F2.wireOp",EDGE,"E4");var subQ16=sQuery(id+"F2.wireOp",EDGE,"E24");var subQ17=sQuery(id+"F0.wireOp",EDGE,"E0.top");var subQ18=sQuery(id+"F2.wireOp",EDGE,"E20.top");var subQ19=sQuery(id+"F2.wireOp",EDGE,"E21");var subQ20=sQuery(id+"F2.wireOp",EDGE,"E23.trimOffspring");var subQ21=sQuery(id+"F2.wireOp",EDGE,"E17.trimOffspring");var subQ22=sQuery(id+"F2.wireOp",EDGE,"E18");var subQ23=sQuery(id+"F2.wireOp",EDGE,"E22");Q0=makeQuery(id+"F7.boolean.opBoolean","SPLIT",FACE,{"disambiguationData":[TD([makeQuery(id+"F1.opExtrude","SWEPT_FACE",FACE,{"disambiguationData":[OSD([subQ14])]})])],"derivedFrom":makeQuery(id+"F6.boolean.opBoolean","MERGE",FACE,{"derivedFrom":[makeQuery(id+"F6.opExtrude","CAP_FACE",FACE,{"disambiguationData":[OSD([sQuery(id+"F2.wireOp",EDGE,"E1.top"),sQuery(id+"F2.wireOp",EDGE,"E1.right"),sQuery(id+"F2.wireOp",EDGE,"E2"),sQuery(id+"F2.wireOp",EDGE,"E3"),sQuery(id+"F2.wireOp",EDGE,"E10"),sQuery(id+"F2.wireOp",EDGE,"E11.trimOffspring"),sQuery(id+"F2.wireOp",EDGE,"E12"),sQuery(id+"F2.wireOp",EDGE,"E13"),sQuery(id+"F2.wireOp",EDGE,"E14.trimOffspring"),subQ18,subQ19,sQuery(id+"F2.wireOp",EDGE,"E25"),subQ12,subQ9,sQuery(id+"F2.wireOp",EDGE,"E28"),sQuery(id+"F2.wireOp",EDGE,"E29"),sQuery(id+"F2.wireOp",EDGE,"E30")])],"isStart":false}),makeQuery(id+"F6.opExtrude","CAP_FACE",FACE,{"disambiguationData":[OSD([subQ15,subQ6,subQ10,subQ21])],"isStart":false}),makeQuery(id+"F6.opExtrude","CAP_FACE",FACE,{"disambiguationData":[OSD([subQ5,subQ4,subQ3,subQ2])],"isStart":false}),makeQuery(id+"F6.opExtrude","CAP_FACE",FACE,{"disambiguationData":[OSD([subQ1,subQ11,subQ8,subQ0,sQuery(id+"F2.wireOp",EDGE,"95qXsgm3-6lwU-iEXp-UI7w-R3bsq3icprrx.bottom"),sQuery(id+"F2.wireOp",EDGE,"95qXsgm3-6lwU-iEXp-UI7w-R3bsq3icprrx.top"),sQuery(id+"F2.wireOp",EDGE,"95qXsgm3-6lwU-iEXp-UI7w-R3bsq3icprrx.left"),sQuery(id+"F2.wireOp",EDGE,"95qXsgm3-6lwU-iEXp-UI7w-R3bsq3icprrx.right")])],"isStart":false}),makeQuery(id+"F6.opExtrude","CAP_FACE",FACE,{"disambiguationData":[OSD([subQ22,subQ23,subQ20,subQ16])],"isStart":false}),makeQuery(id+"F6.opExtrude","CAP_FACE",FACE,{"disambiguationData":[OSD([subQ14,subQ17,subQ13,subQ7])],"isStart":false})]})});}
            var sketch = newSketch(context, id + "F27", { "sketchPlane" : qUnion([Q0])});
            skLineSegment(sketch, "E51.top", {"start": v(15210.48, 23823.75) * mm, "end": v(15100.39, 23823.75) * mm});
            skLineSegment(sketch, "E51.left", {"start": v(15210.48, 26170.67) * mm, "end": v(15210.48, 23823.75) * mm});
            skLineSegment(sketch, "E51.right", {"start": v(15100.39, 26170.67) * mm, "end": v(15100.39, 23823.75) * mm});
            skLineSegment(sketch, "E52.bottom", {"start": v(15210.48, 20823.75) * mm, "end": v(15100.39, 20823.75) * mm});
            skLineSegment(sketch, "E52.top", {"start": v(15210.48, 11533.49) * mm, "end": v(15100.39, 11533.49) * mm});
            skLineSegment(sketch, "E52.left", {"start": v(15210.48, 20823.75) * mm, "end": v(15210.48, 11533.49) * mm});
            skLineSegment(sketch, "E52.right", {"start": v(15100.39, 20823.75) * mm, "end": v(15100.39, 11533.49) * mm});
            skLineSegment(sketch, "E53", {"start": v(15210.48, 26170.67) * mm, "end": v(15100.39, 26170.67) * mm});
            skLineSegment(sketch, "E54.bottom", {"start": v(15100.39, 11533.49) * mm, "end": v(47603.18, 11533.49) * mm});
            skLineSegment(sketch, "E54.top", {"start": v(15100.39, 11783.49) * mm, "end": v(47603.18, 11783.49) * mm});
            skLineSegment(sketch, "E54.left", {"start": v(15100.39, 11533.49) * mm, "end": v(15100.39, 11783.49) * mm});
            skLineSegment(sketch, "E55.bottom", {"start": v(47603.18, 11533.49) * mm, "end": v(47853.18, 11533.49) * mm});
            skLineSegment(sketch, "E55.top", {"start": v(47603.18, 26186.39) * mm, "end": v(47853.18, 26186.39) * mm});
            skLineSegment(sketch, "E55.left", {"start": v(47603.18, 11783.49) * mm, "end": v(47603.18, 26186.39) * mm});
            skLineSegment(sketch, "E55.right", {"start": v(47853.18, 11533.49) * mm, "end": v(47853.18, 26186.39) * mm});
            skSolve(sketch);
        }
        {
            var Q0;
            Q0=makeQuery(id+"F27.imprint","IMPRINT",FACE,{"disambiguationData":[TD([[makeQuery(id+"F27.imprint","IMPRINT",EDGE,{"derivedFrom":sQuery(id+"F27.wireOp",EDGE,"E51.top")}),-1.0]])]});
            var Q1;
            {var subQ5=sQuery(id+"F27.wireOp",EDGE,"E52.bottom");Q1=makeQuery(id+"F27.imprint","IMPRINT",FACE,{"disambiguationData":[TD([[makeQuery(id+"F27.imprint","IMPRINT",EDGE,{"derivedFrom":subQ5}),1.0]])]});}
            extrude(context, id + "F28", {"entities" : qUnion([Q0, Q1]), "operationType" : NewBodyOperationType.ADD, "depth" : 3000 * mm, "offsetDistance" : 25 * mm});
        }
        {
            var Q0;
            {var subQ0=makeQuery(id+"F1.opExtrude","CAP_FACE",FACE,{"disambiguationData":[OSD([sQuery(id+"F0.wireOp",EDGE,"E0.bottom"),sQuery(id+"F0.wireOp",EDGE,"E0.top"),sQuery(id+"F0.wireOp",EDGE,"E0.left"),sQuery(id+"F0.wireOp",EDGE,"E0.right")])],"isStart":false});Q0=makeQuery(id+"F23.boolean.opBoolean","MERGE",FACE,{"derivedFrom":[makeQuery(id+"F19.boolean.opBoolean","MERGE",FACE,{"derivedFrom":[makeQuery(id+"F3.boolean.opBoolean","SPLIT",FACE,{"disambiguationData":[TD([makeQuery(id+"F3.opExtrude","SWEPT_FACE",FACE,{"disambiguationData":[OSD([sQuery(id+"F2.wireOp",EDGE,"E1.top")])]})])],"derivedFrom":subQ0}),makeQuery(id+"F13.boolean.opBoolean","MERGE",FACE,{"derivedFrom":[makeQuery(id+"F3.boolean.opBoolean","SPLIT",FACE,{"disambiguationData":[TD([makeQuery(id+"F3.opExtrude","SWEPT_FACE",FACE,{"disambiguationData":[OSD([sQuery(id+"F2.wireOp",EDGE,"E1.right")])]})])],"derivedFrom":subQ0}),makeQuery(id+"F3.boolean.opBoolean","SPLIT",FACE,{"disambiguationData":[TD([makeQuery(id+"F3.opExtrude","SWEPT_FACE",FACE,{"disambiguationData":[OSD([sQuery(id+"F2.wireOp",EDGE,"E3")])]})])],"derivedFrom":subQ0}),makeQuery(id+"F13.opExtrude","SWEPT_FACE",FACE,{"disambiguationData":[OSD([sQuery(id+"F12.wireOp",EDGE,"E35.top")])]})]}),makeQuery(id+"F19.opExtrude","SWEPT_FACE",FACE,{"disambiguationData":[OSD([sQuery(id+"F18.wireOp",EDGE,"E41.bottom")])]})]}),makeQuery(id+"F23.opExtrude","SWEPT_FACE",FACE,{"disambiguationData":[OSD([sQuery(id+"F22.wireOp",EDGE,"E46.top")])]})]});}
            var sketch = newSketch(context, id + "F29", { "sketchPlane" : qUnion([Q0])});
            skLineSegment(sketch, "E56.left", {"start": v(47250.39, 39211.55) * mm, "end": v(47250.39, 39211.55) * mm});
            skLineSegment(sketch, "E56.right", {"start": v(39250.39, 39211.55) * mm, "end": v(39250.39, 39211.55) * mm});
            skPoint(sketch, "E57.oppositeSnap0", {"position": v(42950.39, 39361.55) * mm});
            skLineSegment(sketch, "E57.bottom", {"start": v(47250.39, 39211.55) * mm, "end": v(39250.39, 39211.55) * mm});
            skLineSegment(sketch, "E57.top", {"start": v(47250.39, 39361.55) * mm, "end": v(39250.39, 39361.55) * mm});
            skLineSegment(sketch, "E57.left", {"start": v(47250.39, 39211.55) * mm, "end": v(47250.39, 39361.55) * mm});
            skLineSegment(sketch, "E57.right", {"start": v(39250.39, 39211.55) * mm, "end": v(39250.39, 39361.55) * mm});
            skSolve(sketch);
        }
        {
            var Q0;
            Q0 = qSketchRegion(id + "F29", true);
            extrude(context, id + "F30", {"entities" : qUnion([Q0]), "operationType" : NewBodyOperationType.ADD, "depth" : 3000 * mm, "offsetDistance" : 25 * mm});
        }
        {
            var Q0;
            Q0=makeQuery(id+"F30.boolean.opBoolean","MERGE",FACE,{"derivedFrom":[makeQuery(id+"F21.opExtrude","SWEPT_FACE",FACE,{"disambiguationData":[OSD([sQuery(id+"F20.wireOp",EDGE,"E43.top")])]}),makeQuery(id+"F30.opExtrude","SWEPT_FACE",FACE,{"disambiguationData":[OSD([sQuery(id+"F29.wireOp",EDGE,"E57.bottom")])]})]});
            var sketch = newSketch(context, id + "F31", { "sketchPlane" : qUnion([Q0])});
            skLineSegment(sketch, "E58.bottom", {"start": v(39465.49, 2525) * mm, "end": v(40465.49, 2525) * mm});
            skLineSegment(sketch, "E58.top", {"start": v(39465.49, 25) * mm, "end": v(40465.49, 25) * mm});
            skLineSegment(sketch, "E58.left", {"start": v(39465.49, 2525) * mm, "end": v(39465.49, 25) * mm});
            skLineSegment(sketch, "E58.right", {"start": v(40465.49, 2525) * mm, "end": v(40465.49, 25) * mm});
            skSolve(sketch);
        }
        {
            var Q0;
            Q0=makeQuery(id+"F31.imprint","IMPRINT",FACE,{"disambiguationData":[TD([[makeQuery(id+"F31.imprint","IMPRINT",EDGE,{"derivedFrom":sQuery(id+"F31.wireOp",EDGE,"E58.bottom")}),-1.0]])]});
            var Q1;
            Q1=sQuery(id+"F31.wireOp",EDGE,"E58.right");
            var Q2;
            Q2=sQuery(id+"F31.wireOp",EDGE,"E58.bottom");
            var Q3;
            Q3=sQuery(id+"F31.wireOp",EDGE,"E58.left");
            var Q4;
            Q4=sQuery(id+"F31.wireOp",EDGE,"E58.top");
            extrude(context, id + "F32", {"entities" : qUnion([Q0]), "operationType" : NewBodyOperationType.REMOVE, "surfaceEntities" : qUnion([Q1, Q2, Q3, Q4]), "oppositeDirection" : true, "depth" : 250 * mm, "offsetDistance" : 25 * mm});
        }
        {
            var Q0;
            Q0 = qSketchRegion(id + "F2", true);
            extrude(context, id + "F33", {"entities" : qUnion([Q0]), "operationType" : NewBodyOperationType.ADD, "depth" : 500 * mm, "offsetDistance" : 25 * mm});
        }
        {
            var Q0;
            Q0=makeQuery(id+"F33.opExtrude","CAP_FACE",FACE,{"disambiguationData":[OSD([sQuery(id+"F2.wireOp",EDGE,"E31.bottom"),sQuery(id+"F2.wireOp",EDGE,"E31.top"),sQuery(id+"F2.wireOp",EDGE,"E31.left"),sQuery(id+"F2.wireOp",EDGE,"E31.right")])],"isStart":false});
            var sketch = newSketch(context, id + "F34", { "sketchPlane" : qUnion([Q0])});
            skCircle(sketch, "E59", {"center": v(17596.24, 24665.55) * mm, "radius": 175 * mm});
            skCircle(sketch, "E60", {"center": v(18112.55, 24665.55) * mm, "radius": 175 * mm});
            skCircle(sketch, "E61", {"center": v(18598.17, 24665.55) * mm, "radius": 175 * mm});
            skCircle(sketch, "E62", {"center": v(19108.49, 24665.55) * mm, "radius": 175 * mm});
            skSolve(sketch);
        }
        {
            var Q0;
            Q0 = qSketchRegion(id + "F34", true);
            extrude(context, id + "F35", {"entities" : qUnion([Q0]), "operationType" : NewBodyOperationType.ADD, "depth" : 12000 * mm, "offsetDistance" : 25 * mm});
        }
        {
            var Q0;
            Q0=makeQuery(id+"F33.opExtrude","CAP_FACE",FACE,{"disambiguationData":[OSD([sQuery(id+"F2.wireOp",EDGE,"E18"),sQuery(id+"F2.wireOp",EDGE,"E22"),sQuery(id+"F2.wireOp",EDGE,"E23.trimOffspring"),sQuery(id+"F2.wireOp",EDGE,"E24")])],"isStart":false});
            var sketch = newSketch(context, id + "F36", { "sketchPlane" : qUnion([Q0])});
            skLineSegment(sketch, "E63.bottom", {"start": v(7100.39, 39420.6) * mm, "end": v(15100.39, 39420.6) * mm});
            skLineSegment(sketch, "E63.top", {"start": v(7100.39, 32919.96) * mm, "end": v(15100.39, 32919.96) * mm});
            skLineSegment(sketch, "E63.left", {"start": v(7100.39, 39420.6) * mm, "end": v(7100.39, 32919.96) * mm});
            skLineSegment(sketch, "E63.right", {"start": v(15100.39, 39420.6) * mm, "end": v(15100.39, 32919.96) * mm});
            skSolve(sketch);
        }
        {
            var Q0;
            Q0 = qSketchRegion(id + "F36", true);
            extrude(context, id + "F37", {"entities" : qUnion([Q0]), "operationType" : NewBodyOperationType.ADD, "depth" : 25 * mm, "offsetDistance" : 25 * mm});
        }
        {
            var Q0;
            {var subQ0=sQuery(id+"F2.wireOp",EDGE,"E23.trimOffspring");var subQ1=sQuery(id+"F2.wireOp",EDGE,"E24");var subQ2=sQuery(id+"F2.wireOp",EDGE,"E18");Q0=makeQuery(id+"F37.boolean.opBoolean","SPLIT",FACE,{"disambiguationData":[TD([makeQuery(id+"F7.opExtrude","SWEPT_FACE",FACE,{"disambiguationData":[OSD([subQ1])]})])],"derivedFrom":makeQuery(id+"F33.opExtrude","CAP_FACE",FACE,{"disambiguationData":[OSD([subQ2,sQuery(id+"F2.wireOp",EDGE,"E22"),subQ0,subQ1])],"isStart":false})});}
            var sketch = newSketch(context, id + "F38", { "sketchPlane" : qUnion([Q0])});
            skLineSegment(sketch, "E64.bottom", {"start": v(10981.19, 37563.28) * mm, "end": v(13148.07, 37563.28) * mm});
            skLineSegment(sketch, "E64.top", {"start": v(10981.19, 34699.9) * mm, "end": v(13148.07, 34699.9) * mm});
            skLineSegment(sketch, "E64.left", {"start": v(10981.19, 37563.28) * mm, "end": v(10981.19, 34699.9) * mm});
            skLineSegment(sketch, "E64.right", {"start": v(13148.07, 37563.28) * mm, "end": v(13148.07, 34699.9) * mm});
            skLineSegment(sketch, "E65.bottom", {"start": v(7653.48, 37640.67) * mm, "end": v(8969.08, 37640.67) * mm});
            skLineSegment(sketch, "E65.top", {"start": v(7653.48, 34699.9) * mm, "end": v(8969.08, 34699.9) * mm});
            skLineSegment(sketch, "E65.left", {"start": v(7653.48, 37640.67) * mm, "end": v(7653.48, 34699.9) * mm});
            skLineSegment(sketch, "E65.right", {"start": v(8969.08, 37640.67) * mm, "end": v(8969.08, 34699.9) * mm});
            skSolve(sketch);
        }
        {
            var Q0;
            Q0 = qSketchRegion(id + "F38", true);
            extrude(context, id + "F39", {"entities" : qUnion([Q0]), "operationType" : NewBodyOperationType.ADD, "depth" : 2500 * mm, "offsetDistance" : 25 * mm});
        }
        {
            var Q0;
            Q0=makeQuery(id+"F26.imprint","IMPRINT",FACE,{"disambiguationData":[TD([[makeQuery(id+"F26.imprint","IMPRINT",EDGE,{"derivedFrom":sQuery(id+"F26.wireOp",EDGE,"E49.bottom")}),-1.0]])]});
            extrude(context, id + "F40", {"entities" : qUnion([Q0]), "depth" : 2800 * mm, "offsetDistance" : 25 * mm});
        }
        {
            var Q0;
            {var subQ4=sQuery(id+"F2.wireOp",EDGE,"E11.trimOffspring");var subQ6=sQuery(id+"F2.wireOp",EDGE,"E1.right");var subQ7=makeQuery(id+"F3.opExtrude","SWEPT_FACE",FACE,{"disambiguationData":[OSD([subQ6])]});var subQ16=makeQuery(id+"F3.opExtrude","SWEPT_FACE",FACE,{"disambiguationData":[OSD([subQ4])]});var subQ18=sQuery(id+"F0.wireOp",EDGE,"E0.top");var subQ26=sQuery(id+"F2.wireOp",EDGE,"E1.top");var subQ27=makeQuery(id+"F3.opExtrude","SWEPT_FACE",FACE,{"disambiguationData":[OSD([subQ26])]});var subQ28=makeQuery(id+"F1.opExtrude","SWEPT_FACE",FACE,{"disambiguationData":[OSD([subQ18])]});var subQ29=makeQuery(id+"F13.opExtrude","SWEPT_FACE",FACE,{"disambiguationData":[OSD([sQuery(id+"F12.wireOp",EDGE,"E35.top")])]});var subQ31=sQuery(id+"F2.wireOp",EDGE,"E3");var subQ32=makeQuery(id+"F3.opExtrude","SWEPT_FACE",FACE,{"disambiguationData":[OSD([subQ31])]});var subQ33=makeQuery(id+"F23.opExtrude","SWEPT_FACE",FACE,{"disambiguationData":[OSD([sQuery(id+"F22.wireOp",EDGE,"E46.top")])]});var subQ36=sQuery(id+"F0.wireOp",EDGE,"E0.right");var subQ37=sQuery(id+"F0.wireOp",EDGE,"E0.left");var subQ38=sQuery(id+"F0.wireOp",EDGE,"E0.bottom");var subQ39=makeQuery(id+"F1.opExtrude","CAP_FACE",FACE,{"disambiguationData":[OSD([subQ38,subQ18,subQ37,subQ36])],"isStart":false});var subQ40=makeQuery(id+"F19.opExtrude","SWEPT_FACE",FACE,{"disambiguationData":[OSD([sQuery(id+"F18.wireOp",EDGE,"E41.bottom")])]});var subQ55=makeQuery(id+"F23.boolean.opBoolean","MERGE",FACE,{"derivedFrom":[makeQuery(id+"F19.boolean.opBoolean","MERGE",FACE,{"derivedFrom":[makeQuery(id+"F3.boolean.opBoolean","SPLIT",FACE,{"disambiguationData":[TD([subQ27])],"derivedFrom":subQ39}),makeQuery(id+"F13.boolean.opBoolean","MERGE",FACE,{"derivedFrom":[makeQuery(id+"F3.boolean.opBoolean","SPLIT",FACE,{"disambiguationData":[TD([subQ7])],"derivedFrom":subQ39}),makeQuery(id+"F3.boolean.opBoolean","SPLIT",FACE,{"disambiguationData":[TD([subQ32])],"derivedFrom":subQ39}),subQ29]}),subQ40]}),subQ33]});Q0=makeQuery(id+"F33.boolean.opBoolean","SPLIT",FACE,{"disambiguationData":[TD([subQ7])],"derivedFrom":makeQuery(id+"F32.boolean.opBoolean","MERGE",FACE,{"derivedFrom":[makeQuery(id+"F30.boolean.opBoolean","SPLIT",FACE,{"disambiguationData":[TD([subQ16])],"derivedFrom":subQ55}),makeQuery(id+"F30.boolean.opBoolean","SPLIT",FACE,{"disambiguationData":[TD([subQ28])],"derivedFrom":subQ55}),makeQuery(id+"F32.opExtrude","SWEPT_FACE",FACE,{"disambiguationData":[OSD([sQuery(id+"F31.wireOp",EDGE,"E58.top")])]})]})});}
            var sketch = newSketch(context, id + "F41", { "sketchPlane" : qUnion([Q0])});
            skLineSegment(sketch, "E66.bottom", {"start": v(43823.5, 41390.39) * mm, "end": v(46095.23, 41390.39) * mm});
            skLineSegment(sketch, "E66.top", {"start": v(43823.5, 40468.52) * mm, "end": v(46095.23, 40468.52) * mm});
            skLineSegment(sketch, "E66.left", {"start": v(43823.5, 41390.39) * mm, "end": v(43823.5, 40468.52) * mm});
            skLineSegment(sketch, "E66.right", {"start": v(46095.23, 41390.39) * mm, "end": v(46095.23, 40468.52) * mm});
            skLineSegment(sketch, "E67.bottom", {"start": v(42535.32, 44155.98) * mm, "end": v(43458.5, 44155.98) * mm});
            skLineSegment(sketch, "E67.top", {"start": v(42535.32, 42283.6) * mm, "end": v(43458.5, 42283.6) * mm});
            skLineSegment(sketch, "E67.left", {"start": v(42535.32, 44155.98) * mm, "end": v(42535.32, 42283.6) * mm});
            skLineSegment(sketch, "E67.right", {"start": v(43458.5, 44155.98) * mm, "end": v(43458.5, 42283.6) * mm});
            skCircle(sketch, "E68", {"center": v(45403.84, 43497.5) * mm, "radius": 739.87 * mm});
            skSolve(sketch);
        }
        {
            var Q0;
            Q0=makeQuery(id+"F41.imprint","IMPRINT",FACE,{"disambiguationData":[TD([[makeQuery(id+"F41.imprint","IMPRINT",EDGE,{"derivedFrom":sQuery(id+"F41.wireOp",EDGE,"E67.bottom")}),-1.0]])]});
            var Q1;
            Q1=makeQuery(id+"F41.imprint","IMPRINT",FACE,{"disambiguationData":[TD([[makeQuery(id+"F41.imprint","IMPRINT",EDGE,{"derivedFrom":sQuery(id+"F41.wireOp",EDGE,"E66.bottom")}),-1.0]])]});
            extrude(context, id + "F42", {"entities" : qUnion([Q0, Q1]), "operationType" : NewBodyOperationType.ADD, "depth" : 1500 * mm, "offsetDistance" : 25 * mm});
        }
        {
            var Q0;
            {var subQ4=sQuery(id+"F2.wireOp",EDGE,"E11.trimOffspring");var subQ6=sQuery(id+"F2.wireOp",EDGE,"E1.right");var subQ7=makeQuery(id+"F3.opExtrude","SWEPT_FACE",FACE,{"disambiguationData":[OSD([subQ6])]});var subQ16=makeQuery(id+"F3.opExtrude","SWEPT_FACE",FACE,{"disambiguationData":[OSD([subQ4])]});var subQ18=sQuery(id+"F0.wireOp",EDGE,"E0.top");var subQ26=sQuery(id+"F2.wireOp",EDGE,"E1.top");var subQ27=makeQuery(id+"F3.opExtrude","SWEPT_FACE",FACE,{"disambiguationData":[OSD([subQ26])]});var subQ28=makeQuery(id+"F1.opExtrude","SWEPT_FACE",FACE,{"disambiguationData":[OSD([subQ18])]});var subQ29=makeQuery(id+"F13.opExtrude","SWEPT_FACE",FACE,{"disambiguationData":[OSD([sQuery(id+"F12.wireOp",EDGE,"E35.top")])]});var subQ31=sQuery(id+"F2.wireOp",EDGE,"E3");var subQ32=makeQuery(id+"F3.opExtrude","SWEPT_FACE",FACE,{"disambiguationData":[OSD([subQ31])]});var subQ33=makeQuery(id+"F23.opExtrude","SWEPT_FACE",FACE,{"disambiguationData":[OSD([sQuery(id+"F22.wireOp",EDGE,"E46.top")])]});var subQ36=sQuery(id+"F0.wireOp",EDGE,"E0.right");var subQ37=sQuery(id+"F0.wireOp",EDGE,"E0.left");var subQ38=sQuery(id+"F0.wireOp",EDGE,"E0.bottom");var subQ39=makeQuery(id+"F1.opExtrude","CAP_FACE",FACE,{"disambiguationData":[OSD([subQ38,subQ18,subQ37,subQ36])],"isStart":false});var subQ40=makeQuery(id+"F19.opExtrude","SWEPT_FACE",FACE,{"disambiguationData":[OSD([sQuery(id+"F18.wireOp",EDGE,"E41.bottom")])]});var subQ55=makeQuery(id+"F23.boolean.opBoolean","MERGE",FACE,{"derivedFrom":[makeQuery(id+"F19.boolean.opBoolean","MERGE",FACE,{"derivedFrom":[makeQuery(id+"F3.boolean.opBoolean","SPLIT",FACE,{"disambiguationData":[TD([subQ27])],"derivedFrom":subQ39}),makeQuery(id+"F13.boolean.opBoolean","MERGE",FACE,{"derivedFrom":[makeQuery(id+"F3.boolean.opBoolean","SPLIT",FACE,{"disambiguationData":[TD([subQ7])],"derivedFrom":subQ39}),makeQuery(id+"F3.boolean.opBoolean","SPLIT",FACE,{"disambiguationData":[TD([subQ32])],"derivedFrom":subQ39}),subQ29]}),subQ40]}),subQ33]});Q0=makeQuery(id+"F33.boolean.opBoolean","SPLIT",FACE,{"disambiguationData":[TD([subQ7])],"derivedFrom":makeQuery(id+"F32.boolean.opBoolean","MERGE",FACE,{"derivedFrom":[makeQuery(id+"F30.boolean.opBoolean","SPLIT",FACE,{"disambiguationData":[TD([subQ16])],"derivedFrom":subQ55}),makeQuery(id+"F30.boolean.opBoolean","SPLIT",FACE,{"disambiguationData":[TD([subQ28])],"derivedFrom":subQ55}),makeQuery(id+"F32.opExtrude","SWEPT_FACE",FACE,{"disambiguationData":[OSD([sQuery(id+"F31.wireOp",EDGE,"E58.top")])]})]})});}
            var sketch = newSketch(context, id + "F43", { "sketchPlane" : qUnion([Q0])});
            skCircle(sketch, "E69", {"center": v(45370.91, 43629.2) * mm, "radius": 618.58 * mm});
            skSolve(sketch);
        }
        {
            var Q0;
            Q0=makeQuery(id+"F43.imprint","IMPRINT",FACE,{"disambiguationData":[TD([[makeQuery(id+"F43.imprint","IMPRINT",EDGE,{"derivedFrom":sQuery(id+"F43.wireOp",EDGE,"E69")}),1.0]])]});
            extrude(context, id + "F44", {"entities" : qUnion([Q0]), "operationType" : NewBodyOperationType.ADD, "depth" : 2500 * mm, "offsetDistance" : 25 * mm});
        }
        {
            var Q0;
            Q0=makeQuery(id+"F44.opExtrude","CAP_EDGE",EDGE,{"disambiguationData":[OSD([sQuery(id+"F43.wireOp",EDGE,"E69")])],"isStart":false});
            fillet(context, id + "F45", {"entities" : qUnion([Q0]), "radius" : 300 * mm, "tangentPropagation" : true, "allowEdgeOverflow" : false});
        }
        {
            var Q0;
            {var subQ7=sQuery(id+"F2.wireOp",EDGE,"E3");var subQ8=makeQuery(id+"F3.opExtrude","SWEPT_FACE",FACE,{"disambiguationData":[OSD([subQ7])]});var subQ14=sQuery(id+"F0.wireOp",EDGE,"E0.top");var subQ16=sQuery(id+"F2.wireOp",EDGE,"E1.right");var subQ17=makeQuery(id+"F3.opExtrude","SWEPT_FACE",FACE,{"disambiguationData":[OSD([subQ16])]});var subQ25=sQuery(id+"F2.wireOp",EDGE,"E1.top");var subQ26=makeQuery(id+"F3.opExtrude","SWEPT_FACE",FACE,{"disambiguationData":[OSD([subQ25])]});var subQ27=makeQuery(id+"F1.opExtrude","SWEPT_FACE",FACE,{"disambiguationData":[OSD([subQ14])]});var subQ28=makeQuery(id+"F13.opExtrude","SWEPT_FACE",FACE,{"disambiguationData":[OSD([sQuery(id+"F12.wireOp",EDGE,"E35.top")])]});var subQ30=makeQuery(id+"F23.opExtrude","SWEPT_FACE",FACE,{"disambiguationData":[OSD([sQuery(id+"F22.wireOp",EDGE,"E46.top")])]});var subQ33=sQuery(id+"F0.wireOp",EDGE,"E0.right");var subQ34=sQuery(id+"F0.wireOp",EDGE,"E0.left");var subQ35=sQuery(id+"F0.wireOp",EDGE,"E0.bottom");var subQ36=makeQuery(id+"F1.opExtrude","CAP_FACE",FACE,{"disambiguationData":[OSD([subQ35,subQ14,subQ34,subQ33])],"isStart":false});var subQ37=makeQuery(id+"F19.opExtrude","SWEPT_FACE",FACE,{"disambiguationData":[OSD([sQuery(id+"F18.wireOp",EDGE,"E41.bottom")])]});var subQ44=sQuery(id+"F2.wireOp",EDGE,"E11.trimOffspring");var subQ51=makeQuery(id+"F3.opExtrude","SWEPT_FACE",FACE,{"disambiguationData":[OSD([subQ44])]});var subQ52=makeQuery(id+"F23.boolean.opBoolean","MERGE",FACE,{"derivedFrom":[makeQuery(id+"F19.boolean.opBoolean","MERGE",FACE,{"derivedFrom":[makeQuery(id+"F3.boolean.opBoolean","SPLIT",FACE,{"disambiguationData":[TD([subQ26])],"derivedFrom":subQ36}),makeQuery(id+"F13.boolean.opBoolean","MERGE",FACE,{"derivedFrom":[makeQuery(id+"F3.boolean.opBoolean","SPLIT",FACE,{"disambiguationData":[TD([subQ17])],"derivedFrom":subQ36}),makeQuery(id+"F3.boolean.opBoolean","SPLIT",FACE,{"disambiguationData":[TD([subQ8])],"derivedFrom":subQ36}),subQ28]}),subQ37]}),subQ30]});Q0=makeQuery(id+"F33.boolean.opBoolean","SPLIT",FACE,{"disambiguationData":[TD([subQ8])],"derivedFrom":makeQuery(id+"F32.boolean.opBoolean","MERGE",FACE,{"derivedFrom":[makeQuery(id+"F30.boolean.opBoolean","SPLIT",FACE,{"disambiguationData":[TD([subQ51])],"derivedFrom":subQ52}),makeQuery(id+"F30.boolean.opBoolean","SPLIT",FACE,{"disambiguationData":[TD([subQ27])],"derivedFrom":subQ52}),makeQuery(id+"F32.opExtrude","SWEPT_FACE",FACE,{"disambiguationData":[OSD([sQuery(id+"F31.wireOp",EDGE,"E58.top")])]})]})});}
            var sketch = newSketch(context, id + "F46", { "sketchPlane" : qUnion([Q0])});
            skLineSegment(sketch, "E70.bottom", {"start": v(34673.04, 44489.85) * mm, "end": v(34903.12, 44489.85) * mm});
            skLineSegment(sketch, "E70.top", {"start": v(34673.04, 39489.85) * mm, "end": v(34903.12, 39489.85) * mm});
            skLineSegment(sketch, "E70.left", {"start": v(34673.04, 44489.85) * mm, "end": v(34673.04, 39489.85) * mm});
            skLineSegment(sketch, "E70.right", {"start": v(34903.12, 44489.85) * mm, "end": v(34903.12, 39489.85) * mm});
            skSolve(sketch);
        }
        {
            var Q0;
            Q0=makeQuery(id+"F46.imprint","IMPRINT",FACE,{"disambiguationData":[TD([[makeQuery(id+"F46.imprint","IMPRINT",EDGE,{"derivedFrom":sQuery(id+"F46.wireOp",EDGE,"E70.bottom")}),1.0]])]});
            extrude(context, id + "F47", {"entities" : qUnion([Q0]), "operationType" : NewBodyOperationType.ADD, "depth" : 3000 * mm, "offsetDistance" : 25 * mm});
        }
        {
            var Q0;
            {var subQ0=sQuery(id+"F2.wireOp",EDGE,"E27");Q0=makeQuery(id+"F33.boolean.opBoolean","MERGE",FACE,{"derivedFrom":[makeQuery(id+"F3.opExtrude","SWEPT_FACE",FACE,{"disambiguationData":[OSD([subQ0])]}),makeQuery(id+"F33.opExtrude","SWEPT_FACE",FACE,{"disambiguationData":[OSD([subQ0])]})]});}
            var sketch = newSketch(context, id + "F48", { "sketchPlane" : qUnion([Q0])});
            skLineSegment(sketch, "E71.bottom", {"start": v(47550.39, 3025) * mm, "end": v(39050.39, 3025) * mm});
            skLineSegment(sketch, "E71.top", {"start": v(47550.39, 2990) * mm, "end": v(39050.39, 2990) * mm});
            skLineSegment(sketch, "E71.left", {"start": v(47550.39, 3025) * mm, "end": v(47550.39, 2990) * mm});
            skLineSegment(sketch, "E71.right", {"start": v(39050.39, 3025) * mm, "end": v(39050.39, 2990) * mm});
            skSolve(sketch);
        }
        {
            var Q0;
            Q0=makeQuery(id+"F3.opExtrude","CAP_FACE",FACE,{"disambiguationData":[OSD([sQuery(id+"F2.wireOp",EDGE,"E1.top"),sQuery(id+"F2.wireOp",EDGE,"E1.right"),sQuery(id+"F2.wireOp",EDGE,"E2"),sQuery(id+"F2.wireOp",EDGE,"E3"),sQuery(id+"F2.wireOp",EDGE,"E10"),sQuery(id+"F2.wireOp",EDGE,"E11.trimOffspring"),sQuery(id+"F2.wireOp",EDGE,"E12"),sQuery(id+"F2.wireOp",EDGE,"E13"),sQuery(id+"F2.wireOp",EDGE,"E14.trimOffspring"),sQuery(id+"F2.wireOp",EDGE,"E20.top"),sQuery(id+"F2.wireOp",EDGE,"E21"),sQuery(id+"F2.wireOp",EDGE,"E25"),sQuery(id+"F2.wireOp",EDGE,"E26"),sQuery(id+"F2.wireOp",EDGE,"E27"),sQuery(id+"F2.wireOp",EDGE,"E28"),sQuery(id+"F2.wireOp",EDGE,"E29"),sQuery(id+"F2.wireOp",EDGE,"E30")])],"isStart":false});
            var sketch = newSketch(context, id + "F49", { "sketchPlane" : qUnion([Q0])});
            skLineSegment(sketch, "E72.bottom", {"start": v(36007.2, 44789.85) * mm, "end": v(42007.2, 44789.85) * mm});
            skLineSegment(sketch, "E72.top", {"start": v(36007.2, 40789.85) * mm, "end": v(42007.2, 40789.85) * mm});
            skLineSegment(sketch, "E72.left", {"start": v(36007.2, 44789.85) * mm, "end": v(36007.2, 40789.85) * mm});
            skLineSegment(sketch, "E72.right", {"start": v(42007.2, 44789.85) * mm, "end": v(42007.2, 40789.85) * mm});
            skSolve(sketch);
        }
        {
            var Q0;
            Q0 = qSketchRegion(id + "F49", true);
            extrude(context, id + "F50", {"entities" : qUnion([Q0]), "operationType" : NewBodyOperationType.ADD, "depth" : 25 * mm, "offsetDistance" : 25 * mm});
        }
        {
            var Q0;
            Q0=makeQuery(id+"F50.opExtrude","CAP_FACE",FACE,{"disambiguationData":[OSD([sQuery(id+"F49.wireOp",EDGE,"E72.bottom"),sQuery(id+"F49.wireOp",EDGE,"E72.top"),sQuery(id+"F49.wireOp",EDGE,"E72.left"),sQuery(id+"F49.wireOp",EDGE,"E72.right")])],"isStart":false});
            var sketch = newSketch(context, id + "F51", { "sketchPlane" : qUnion([Q0])});
            skLineSegment(sketch, "E73.bottom", {"start": v(36188.47, 44429.99) * mm, "end": v(41819.86, 44429.99) * mm});
            skLineSegment(sketch, "E73.top", {"start": v(36188.47, 43829.92) * mm, "end": v(41819.86, 43829.92) * mm});
            skLineSegment(sketch, "E73.left", {"start": v(36188.47, 44429.99) * mm, "end": v(36188.47, 43829.92) * mm});
            skLineSegment(sketch, "E73.right", {"start": v(41819.86, 44429.99) * mm, "end": v(41819.86, 43829.92) * mm});
            skLineSegment(sketch, "E74.bottom", {"start": v(38242.55, 42814.42) * mm, "end": v(39881.19, 42814.42) * mm});
            skLineSegment(sketch, "E74.top", {"start": v(38242.55, 40789.85) * mm, "end": v(39881.19, 40789.85) * mm});
            skLineSegment(sketch, "E74.left", {"start": v(38242.55, 42814.42) * mm, "end": v(38242.55, 40789.85) * mm});
            skLineSegment(sketch, "E74.right", {"start": v(39881.19, 42814.42) * mm, "end": v(39881.19, 40789.85) * mm});
            skLineSegment(sketch, "E75", {"start": v(39061.87, 42814.42) * mm, "end": v(39061.87, 40789.85) * mm});
            skSolve(sketch);
        }
        {
            var Q0;
            Q0 = qSketchRegion(id + "F51", true);
            extrude(context, id + "F52", {"entities" : qUnion([Q0]), "operationType" : NewBodyOperationType.ADD, "depth" : 25 * mm, "offsetDistance" : 25 * mm});
        }
        {
            var Q0;
            {var subQ6=sQuery(id+"F2.wireOp",EDGE,"E1.top");var subQ7=makeQuery(id+"F3.opExtrude","SWEPT_FACE",FACE,{"disambiguationData":[OSD([subQ6])]});var subQ8=sQuery(id+"F0.wireOp",EDGE,"E0.top");var subQ10=sQuery(id+"F2.wireOp",EDGE,"E1.right");var subQ11=makeQuery(id+"F3.opExtrude","SWEPT_FACE",FACE,{"disambiguationData":[OSD([subQ10])]});var subQ17=makeQuery(id+"F1.opExtrude","SWEPT_FACE",FACE,{"disambiguationData":[OSD([subQ8])]});var subQ18=sQuery(id+"F2.wireOp",EDGE,"E3");var subQ19=makeQuery(id+"F3.opExtrude","SWEPT_FACE",FACE,{"disambiguationData":[OSD([subQ18])]});var subQ20=makeQuery(id+"F23.opExtrude","SWEPT_FACE",FACE,{"disambiguationData":[OSD([sQuery(id+"F22.wireOp",EDGE,"E46.top")])]});var subQ22=sQuery(id+"F0.wireOp",EDGE,"E0.right");var subQ23=sQuery(id+"F0.wireOp",EDGE,"E0.left");var subQ24=sQuery(id+"F0.wireOp",EDGE,"E0.bottom");var subQ25=makeQuery(id+"F1.opExtrude","CAP_FACE",FACE,{"disambiguationData":[OSD([subQ24,subQ8,subQ23,subQ22])],"isStart":false});var subQ36=sQuery(id+"F2.wireOp",EDGE,"E11.trimOffspring");var subQ43=makeQuery(id+"F3.opExtrude","SWEPT_FACE",FACE,{"disambiguationData":[OSD([subQ36])]});var subQ44=makeQuery(id+"F23.boolean.opBoolean","MERGE",FACE,{"derivedFrom":[makeQuery(id+"F19.boolean.opBoolean","MERGE",FACE,{"derivedFrom":[makeQuery(id+"F3.boolean.opBoolean","SPLIT",FACE,{"disambiguationData":[TD([subQ7])],"derivedFrom":subQ25}),makeQuery(id+"F13.boolean.opBoolean","MERGE",FACE,{"derivedFrom":[makeQuery(id+"F3.boolean.opBoolean","SPLIT",FACE,{"disambiguationData":[TD([subQ11])],"derivedFrom":subQ25}),makeQuery(id+"F3.boolean.opBoolean","SPLIT",FACE,{"disambiguationData":[TD([subQ19])],"derivedFrom":subQ25})],"fromTools":[makeQuery(id+"F13.opExtrude","SWEPT_FACE",FACE,{"disambiguationData":[OSD([sQuery(id+"F12.wireOp",EDGE,"E35.top")])]})]})],"fromTools":[makeQuery(id+"F19.opExtrude","SWEPT_FACE",FACE,{"disambiguationData":[OSD([sQuery(id+"F18.wireOp",EDGE,"E41.bottom")])]})]})],"fromTools":[subQ20]});Q0=makeQuery(id+"F33.boolean.opBoolean","SPLIT",FACE,{"disambiguationData":[TD([subQ7])],"derivedFrom":makeQuery(id+"F32.boolean.opBoolean","MERGE",FACE,{"derivedFrom":[makeQuery(id+"F30.boolean.opBoolean","SPLIT",FACE,{"disambiguationData":[TD([subQ43])],"derivedFrom":subQ44}),makeQuery(id+"F30.boolean.opBoolean","SPLIT",FACE,{"disambiguationData":[TD([subQ17])],"derivedFrom":subQ44})],"fromTools":[makeQuery(id+"F32.opExtrude","SWEPT_FACE",FACE,{"disambiguationData":[OSD([sQuery(id+"F31.wireOp",EDGE,"E58.top")])]})]})});}
            var sketch = newSketch(context, id + "F53", { "sketchPlane" : qUnion([Q0])});
            skLineSegment(sketch, "E76.bottom", {"start": v(17606.17, 34231.88) * mm, "end": v(20789, 34231.88) * mm});
            skLineSegment(sketch, "E76.top", {"start": v(17606.17, 27943.88) * mm, "end": v(20789, 27943.88) * mm});
            skLineSegment(sketch, "E76.left", {"start": v(17606.17, 34231.88) * mm, "end": v(17606.17, 27943.88) * mm});
            skLineSegment(sketch, "E76.right", {"start": v(20789, 34231.88) * mm, "end": v(20789, 27943.88) * mm});
            skLineSegment(sketch, "E77.bottom", {"start": v(23195.51, 34231.88) * mm, "end": v(26455.96, 34231.88) * mm});
            skLineSegment(sketch, "E77.top", {"start": v(23195.51, 27943.88) * mm, "end": v(26455.96, 27943.88) * mm});
            skLineSegment(sketch, "E77.left", {"start": v(23195.51, 34231.88) * mm, "end": v(23195.51, 27943.88) * mm});
            skLineSegment(sketch, "E77.right", {"start": v(26455.96, 34231.88) * mm, "end": v(26455.96, 27943.88) * mm});
            skLineSegment(sketch, "E78.bottom", {"start": v(28551.97, 27943.88) * mm, "end": v(31890.05, 27943.88) * mm});
            skLineSegment(sketch, "E78.top", {"start": v(28551.97, 34231.88) * mm, "end": v(31890.05, 34231.88) * mm});
            skLineSegment(sketch, "E78.left", {"start": v(28551.97, 27943.88) * mm, "end": v(28551.97, 34231.88) * mm});
            skLineSegment(sketch, "E78.right", {"start": v(31890.05, 27943.88) * mm, "end": v(31890.05, 34231.88) * mm});
            skLineSegment(sketch, "E79.bottom", {"start": v(33753.16, 34231.88) * mm, "end": v(37013.6, 34231.88) * mm});
            skLineSegment(sketch, "E79.top", {"start": v(33753.16, 27943.88) * mm, "end": v(37013.6, 27943.88) * mm});
            skLineSegment(sketch, "E79.left", {"start": v(33753.16, 34231.88) * mm, "end": v(33753.16, 27943.88) * mm});
            skLineSegment(sketch, "E79.right", {"start": v(37013.6, 34231.88) * mm, "end": v(37013.6, 27943.88) * mm});
            skSolve(sketch);
        }
        {
            var Q0;
            Q0 = qSketchRegion(id + "F53", true);
            extrude(context, id + "F54", {"entities" : qUnion([Q0]), "operationType" : NewBodyOperationType.ADD, "depth" : 3000 * mm, "offsetDistance" : 25 * mm});
        }
    });
